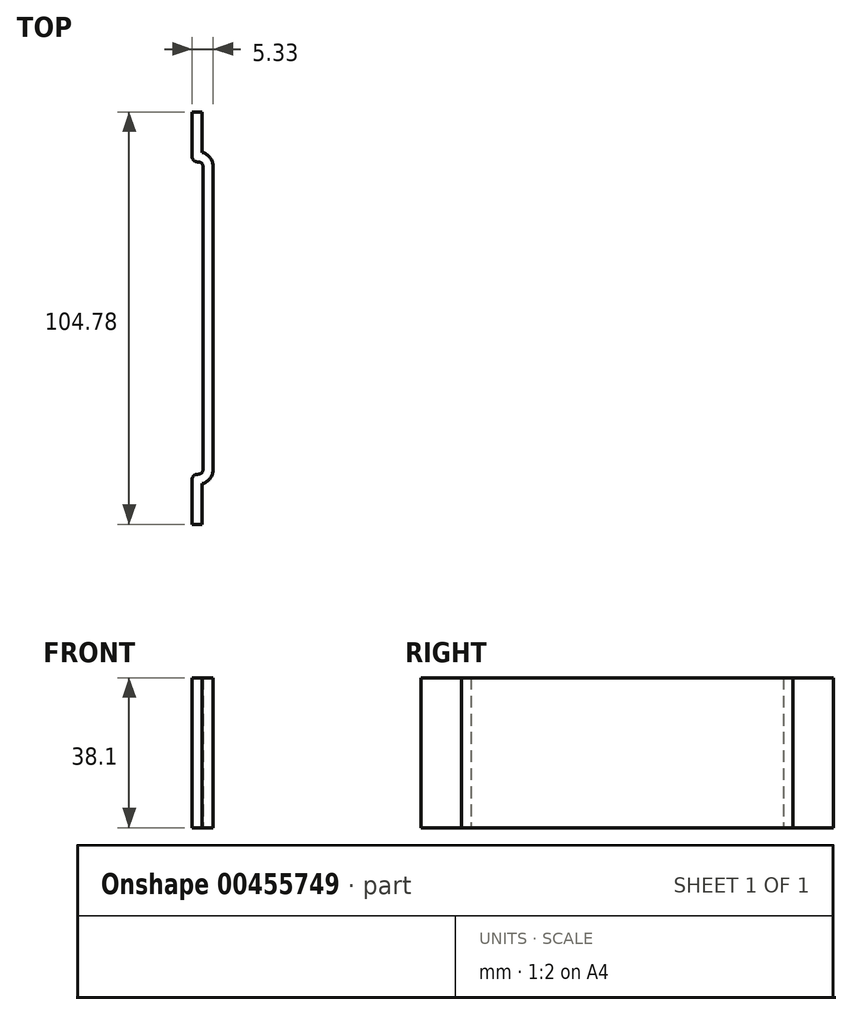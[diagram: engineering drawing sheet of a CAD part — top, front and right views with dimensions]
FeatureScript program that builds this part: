
annotation { "Feature Type Name" : "Feature", "Feature Type Description" : "" }
export const myFeature = defineFeature(function(context is Context, id is Id, definition is map)
    precondition{}
    {
        {
            var Q0;
            Q0=qCreatedBy(makeId("Top.planeOp"),FACE);
            var sketch = newSketch(context, id + "F0", { "sketchPlane" : qUnion([Q0])});
            skLineSegment(sketch, "E0", {"start": v(0, -40.96) * mm, "end": v(0, -52.39) * mm});
            skLineSegment(sketch, "E1", {"start": v(1.27, -39.69) * mm, "end": v(1.52, -39.69) * mm});
            skLineSegment(sketch, "E2", {"start": v(2.8, -38.42) * mm, "end": v(2.8, 0) * mm});
            skPoint(sketch, "E3.visualSharp", {"position": v(0, -39.69) * mm});
            skArc(sketch, "E3.filletArc", {"start": v(1.27, -39.69) * mm, "mid": v(0.37, -40.06) * mm, "end": v(0, -40.96) * mm});
            skPoint(sketch, "E4.visualSharp", {"position": v(2.8, -39.69) * mm});
            skArc(sketch, "E4.filletArc", {"start": v(1.52, -39.69) * mm, "mid": v(2.42, -39.32) * mm, "end": v(2.8, -38.42) * mm});
            skLineSegment(sketch, "E5", {"start": v(0, 0) * mm, "end": v(35.98, 0) * mm, "construction": true});
            skLineSegment(sketch, "E6.MirrorCS", {"start": v(0, 40.96) * mm, "end": v(0, 52.39) * mm});
            skPoint(sketch, "E7.MirrorP", {"position": v(0, 39.69) * mm});
            skLineSegment(sketch, "E8.MirrorCS", {"start": v(2.8, 38.42) * mm, "end": v(2.8, 0) * mm});
            skArc(sketch, "E9.MirrorCS", {"start": v(1.27, 39.69) * mm, "mid": v(0.37, 40.06) * mm, "end": v(0, 40.96) * mm});
            skLineSegment(sketch, "E10.MirrorCS", {"start": v(1.27, 39.69) * mm, "end": v(1.52, 39.69) * mm});
            skArc(sketch, "E11.MirrorCS", {"start": v(1.52, 39.69) * mm, "mid": v(2.42, 39.32) * mm, "end": v(2.8, 38.42) * mm});
            skLineSegment(sketch, "E12.0", {"start": v(2.54, -42.09) * mm, "end": v(2.54, -52.39) * mm});
            skArc(sketch, "E12.1", {"start": v(2.54, -42.09) * mm, "mid": v(4.56, -40.72) * mm, "end": v(5.33, -38.42) * mm});
            skLineSegment(sketch, "E12.2", {"start": v(2.54, 42.09) * mm, "end": v(2.54, 52.39) * mm});
            skArc(sketch, "E12.3", {"start": v(2.54, 42.09) * mm, "mid": v(4.56, 40.72) * mm, "end": v(5.33, 38.42) * mm});
            skLineSegment(sketch, "E12.4", {"start": v(5.33, 38.42) * mm, "end": v(5.33, 0) * mm});
            skLineSegment(sketch, "E12.5", {"start": v(5.33, -38.42) * mm, "end": v(5.33, 0) * mm});
            skLineSegment(sketch, "E13", {"start": v(2.54, 52.39) * mm, "end": v(0, 52.39) * mm});
            skLineSegment(sketch, "E14", {"start": v(2.54, -52.39) * mm, "end": v(0, -52.39) * mm});
            skSolve(sketch);
        }
        {
            var Q0;
            Q0 = qSketchRegion(id + "F0", true);
            extrude(context, id + "F1", {"entities" : qUnion([Q0]), "depth" : 38.1 * mm});
        }
    });
